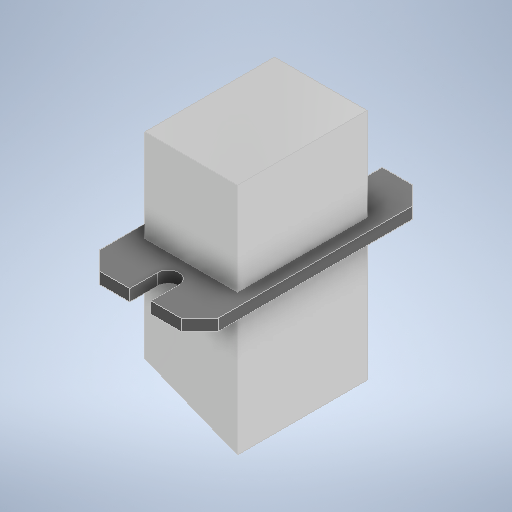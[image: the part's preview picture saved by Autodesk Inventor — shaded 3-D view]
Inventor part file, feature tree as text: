
AUTODESK INVENTOR PART (.ipt)
format: ipt  version: 2025 (Build 290162000, 162)  size: 276,992 bytes
history: native  units: mm
features: extrude x4, sketch x4
ambient origin geometry x8: Origin, YZ Plane, XZ Plane, XY Plane, X Axis, Y Axis, Z Axis, Center Point
bodies: Solid1 (feature_tree)
feature tree (8):
  extrude  "Extrusion1"  Depth=12.8mm
  extrude  "Extrusion2"  Depth=2.0mm
  extrude  "Extrusion3"  Depth=2.0mm
  extrude  "Extrusion4"  Depth=14.0mm
  sketch  "Sketch1"  dims[d0=25.0mm d1=12.8mm]
  sketch  "Sketch2"  dims[d2=2.0mm d3=2.0mm]
  sketch  "Sketch3"  dims[d4=2.0mm d5=2.0mm]
  sketch  "Sketch4"  dims[d6=2.0mm d7=2.0mm d8=2.0mm d9=2.0mm d10=2.3mm d11=2.3mm d12=3.0mm d13=3.0mm d14=1.25mm d15=0.0mm d16=10.0mm d17=14.0mm d18=10.0mm d19=0.0mm d20=10.0mm d21=14.0mm d22=14.0mm d23=0.0mm d24=4.0mm d25=0.0mm d26=0.0mm]
